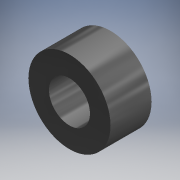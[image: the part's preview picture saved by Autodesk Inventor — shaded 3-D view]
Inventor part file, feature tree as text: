
AUTODESK INVENTOR PART (.ipt)
format: ipt  version: 2019 (Build 230136000, 136)  size: 90,112 bytes
history: native  units: mm (DEFAULTED — no unit token found)
features: extrude x1, sketch x1
ambient origin geometry x8: Origin, YZ Plane, XZ Plane, XY Plane, X Axis, Y Axis, Z Axis, Center Point
bodies: Solid1 (feature_tree)
feature tree (2):
  extrude  "Extrusion1"  Depth=5.08mm
  sketch  "Sketch1"  dims[d0=5.08mm d1=10.16mm d2=5.08mm d3=0.0mm]
